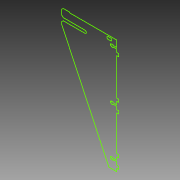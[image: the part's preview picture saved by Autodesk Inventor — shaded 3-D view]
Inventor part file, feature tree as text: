
AUTODESK INVENTOR PART (.ipt)
format: ipt  version: 2015 (Build 190159000, 159)  size: 90,112 bytes
history: native  units: mm
features: sketch x1
ambient origin geometry x8: Origin, YZ Plane, XZ Plane, XY Plane, X Axis, Y Axis, Z Axis, Center Point
feature tree (1):
  sketch  "Sketch1"
